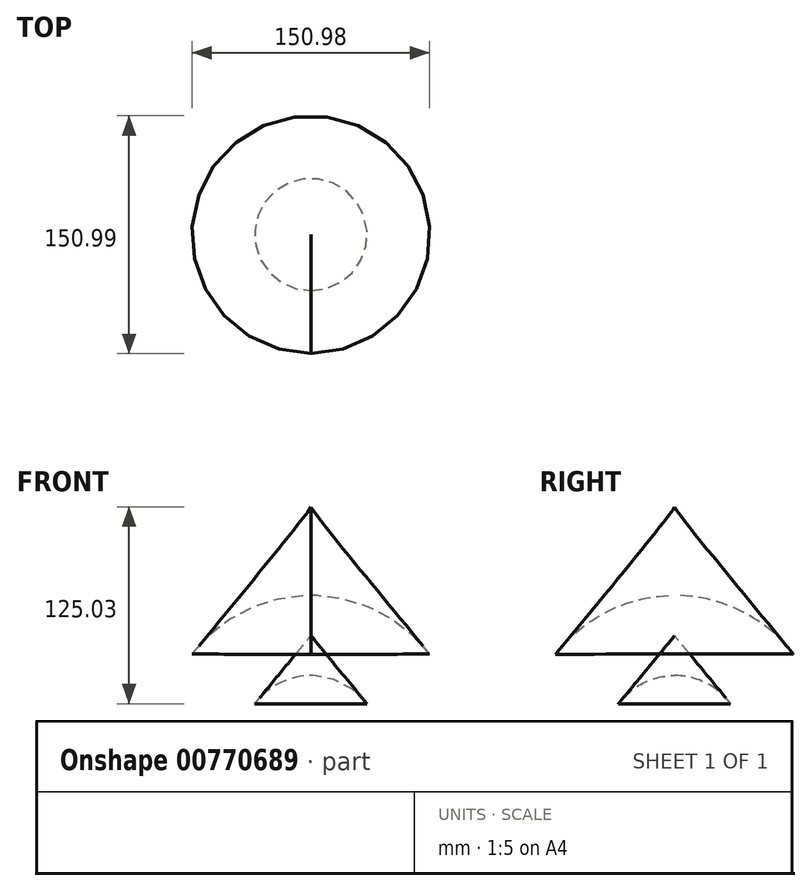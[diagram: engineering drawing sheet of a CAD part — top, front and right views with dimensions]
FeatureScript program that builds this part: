
annotation { "Feature Type Name" : "Feature", "Feature Type Description" : "" }
export const myFeature = defineFeature(function(context is Context, id is Id, definition is map)
    precondition{}
    {
        {
            var Q0;
            Q0=qCreatedBy(makeId("Right.planeOp"),FACE);
            var sketch = newSketch(context, id + "F0", { "sketchPlane" : qUnion([Q0])});
            skArc(sketch, "E0", {"start": v(-75.48, 0) * mm, "mid": v(0.02, -153.08) * mm, "end": v(75.52, 0) * mm});
            skFitSpline(sketch, "E1", {"points": [v(-75.48, 0) * mm, v(0, 93.52) * mm, v(0, 93.87) * mm], "startDerivative": vector(117.3, 142.08) * mm, "endDerivative": vector(-2.04, 4.5) * mm});
            skFitSpline(sketch, "E2", {"points": [v(0, 93.87) * mm, v(75.52, 0) * mm], "startDerivative": vector(75.52, -93.87) * mm, "endDerivative": vector(75.52, -93.87) * mm});
            skLineSegment(sketch, "E3", {"start": v(0, 93.52) * mm, "end": v(0.03, -153.08) * mm});
            skSolve(sketch);
        }
        {
            var Q0;
            {var subQ3=sQuery(id+"F0.wireOp",EDGE,"E3");Q0=makeQuery(id+"F0.imprint","IMPRINT",FACE,{"disambiguationData":[TD([[makeQuery(id+"F0.imprint","IMPRINT",EDGE,{"derivedFrom":subQ3}),-1.0]])]});}
            var Q1;
            Q1=sQuery(id+"F0.wireOp",EDGE,"E3");
            revolve(context, id + "F1", {"surfaceOperationType" : NewSurfaceOperationType.NEW, "entities" : qUnion([Q0]), "axis" : qUnion([Q1]), "revolveType" : RevolveType.FULL});
        }
        {
            var Q0;
            Q0=makeQuery(id+"F1.opRevolve","SWEPT_FACE",FACE,{"disambiguationData":[OSD([sQuery(id+"F0.wireOp",EDGE,"E1")])]});
            var Q1;
            Q1=makeQuery(id+"F1.opRevolve","SWEPT_BODY",BODY,{"disambiguationData":[OSD([sQuery(id+"F0.wireOp",EDGE,"E0"),sQuery(id+"F0.wireOp",EDGE,"E1"),sQuery(id+"F0.wireOp",EDGE,"E3")])]});
            shell(context, id + "F2", {"isHollow" : true, "entities" : qUnion([Q0]), "parts" : qUnion([Q1]), "thickness" : 50.8 * mm});
        }
    });
